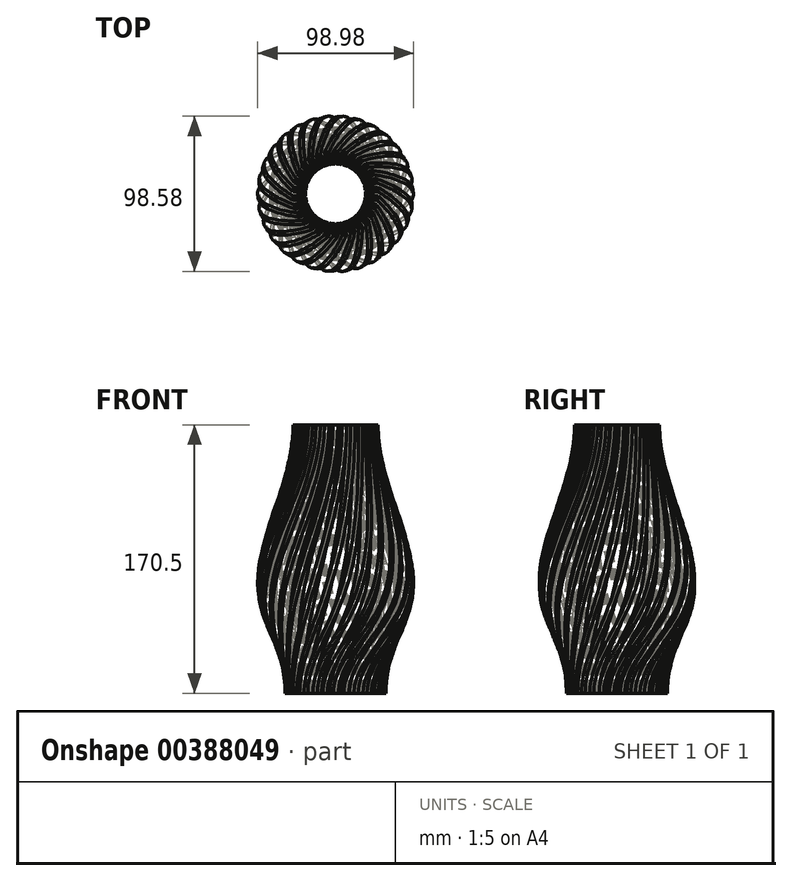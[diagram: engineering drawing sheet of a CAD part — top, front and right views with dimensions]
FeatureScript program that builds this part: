
annotation { "Feature Type Name" : "Feature", "Feature Type Description" : "" }
export const myFeature = defineFeature(function(context is Context, id is Id, definition is map)
    precondition{}
    {
        {
            var Q0;
            Q0=qCreatedBy(makeId("Top.planeOp"),FACE);
            var sketch = newSketch(context, id + "F0", { "sketchPlane" : qUnion([Q0])});
            skCircle(sketch, "E0", {"center": v(0, 0) * mm, "radius": 25 * mm});
            skLineSegment(sketch, "E1", {"start": v(-1.5, 24.95) * mm, "end": v(-1.5, 31.95) * mm});
            skLineSegment(sketch, "E2", {"start": v(-1.5, 31.95) * mm, "end": v(1.5, 31.95) * mm});
            skLineSegment(sketch, "E3", {"start": v(1.5, 31.95) * mm, "end": v(1.5, 24.95) * mm});
            skLineSegment(sketch, "E4", {"start": v(0, 25) * mm, "end": v(0, 35.88) * mm, "construction": true});
            skLineSegment(sketch, "E5.1.0", {"start": v(-5.18, 31.57) * mm, "end": v(-3.72, 24.72) * mm});
            skLineSegment(sketch, "E5.1.1", {"start": v(-8.11, 30.94) * mm, "end": v(-5.18, 31.57) * mm});
            skLineSegment(sketch, "E5.1.2", {"start": v(-6.66, 24.1) * mm, "end": v(-8.11, 30.94) * mm});
            skLineSegment(sketch, "E5.2.0", {"start": v(-11.63, 29.8) * mm, "end": v(-8.78, 23.4) * mm});
            skLineSegment(sketch, "E5.2.1", {"start": v(-14.37, 28.58) * mm, "end": v(-11.63, 29.8) * mm});
            skLineSegment(sketch, "E5.2.2", {"start": v(-11.52, 22.19) * mm, "end": v(-14.37, 28.58) * mm});
            skLineSegment(sketch, "E5.3.0", {"start": v(-17.57, 26.73) * mm, "end": v(-13.45, 21.07) * mm});
            skLineSegment(sketch, "E5.3.1", {"start": v(-20, 24.97) * mm, "end": v(-17.57, 26.73) * mm});
            skLineSegment(sketch, "E5.3.2", {"start": v(-15.88, 19.3) * mm, "end": v(-20, 24.97) * mm});
            skLineSegment(sketch, "E5.4.0", {"start": v(-22.74, 22.5) * mm, "end": v(-17.54, 17.81) * mm});
            skLineSegment(sketch, "E5.4.1", {"start": v(-24.75, 20.27) * mm, "end": v(-22.74, 22.5) * mm});
            skLineSegment(sketch, "E5.4.2", {"start": v(-19.55, 15.58) * mm, "end": v(-24.75, 20.27) * mm});
            skLineSegment(sketch, "E5.5.0", {"start": v(-26.92, 17.28) * mm, "end": v(-20.86, 13.78) * mm});
            skLineSegment(sketch, "E5.5.1", {"start": v(-28.42, 14.68) * mm, "end": v(-26.92, 17.28) * mm});
            skLineSegment(sketch, "E5.5.2", {"start": v(-22.36, 11.18) * mm, "end": v(-28.42, 14.68) * mm});
            skLineSegment(sketch, "E5.6.0", {"start": v(-29.93, 11.3) * mm, "end": v(-23.27, 9.14) * mm});
            skLineSegment(sketch, "E5.6.1", {"start": v(-30.85, 8.45) * mm, "end": v(-29.93, 11.3) * mm});
            skLineSegment(sketch, "E5.6.2", {"start": v(-24.2, 6.28) * mm, "end": v(-30.85, 8.45) * mm});
            skLineSegment(sketch, "E5.7.0", {"start": v(-31.62, 4.83) * mm, "end": v(-24.66, 4.1) * mm});
            skLineSegment(sketch, "E5.7.1", {"start": v(-31.94, 1.85) * mm, "end": v(-31.62, 4.83) * mm});
            skLineSegment(sketch, "E5.7.2", {"start": v(-24.98, 1.12) * mm, "end": v(-31.94, 1.85) * mm});
            skLineSegment(sketch, "E5.8.0", {"start": v(-31.94, -1.85) * mm, "end": v(-24.98, -1.12) * mm});
            skLineSegment(sketch, "E5.8.1", {"start": v(-31.62, -4.83) * mm, "end": v(-31.94, -1.85) * mm});
            skLineSegment(sketch, "E5.8.2", {"start": v(-24.66, -4.1) * mm, "end": v(-31.62, -4.83) * mm});
            skLineSegment(sketch, "E5.9.0", {"start": v(-30.85, -8.45) * mm, "end": v(-24.2, -6.28) * mm});
            skLineSegment(sketch, "E5.9.1", {"start": v(-29.93, -11.3) * mm, "end": v(-30.85, -8.45) * mm});
            skLineSegment(sketch, "E5.9.2", {"start": v(-23.27, -9.14) * mm, "end": v(-29.93, -11.3) * mm});
            skLineSegment(sketch, "E5.10.0", {"start": v(-28.42, -14.68) * mm, "end": v(-22.36, -11.18) * mm});
            skLineSegment(sketch, "E5.10.1", {"start": v(-26.92, -17.28) * mm, "end": v(-28.42, -14.68) * mm});
            skLineSegment(sketch, "E5.10.2", {"start": v(-20.86, -13.78) * mm, "end": v(-26.92, -17.28) * mm});
            skLineSegment(sketch, "E5.11.0", {"start": v(-24.75, -20.27) * mm, "end": v(-19.55, -15.58) * mm});
            skLineSegment(sketch, "E5.11.1", {"start": v(-22.74, -22.5) * mm, "end": v(-24.75, -20.27) * mm});
            skLineSegment(sketch, "E5.11.2", {"start": v(-17.54, -17.81) * mm, "end": v(-22.74, -22.5) * mm});
            skLineSegment(sketch, "E5.12.0", {"start": v(-20, -24.97) * mm, "end": v(-15.88, -19.3) * mm});
            skLineSegment(sketch, "E5.12.1", {"start": v(-17.57, -26.73) * mm, "end": v(-20, -24.97) * mm});
            skLineSegment(sketch, "E5.12.2", {"start": v(-13.45, -21.07) * mm, "end": v(-17.57, -26.73) * mm});
            skLineSegment(sketch, "E5.13.0", {"start": v(-14.37, -28.58) * mm, "end": v(-11.52, -22.19) * mm});
            skLineSegment(sketch, "E5.13.1", {"start": v(-11.63, -29.8) * mm, "end": v(-14.37, -28.58) * mm});
            skLineSegment(sketch, "E5.13.2", {"start": v(-8.78, -23.4) * mm, "end": v(-11.63, -29.8) * mm});
            skLineSegment(sketch, "E5.14.0", {"start": v(-8.11, -30.94) * mm, "end": v(-6.66, -24.1) * mm});
            skLineSegment(sketch, "E5.14.1", {"start": v(-5.18, -31.57) * mm, "end": v(-8.11, -30.94) * mm});
            skLineSegment(sketch, "E5.14.2", {"start": v(-3.72, -24.72) * mm, "end": v(-5.18, -31.57) * mm});
            skLineSegment(sketch, "E6.2.15.0", {"start": v(-1.5, -31.95) * mm, "end": v(-1.5, -24.95) * mm});
            skLineSegment(sketch, "E6.3.15.0", {"start": v(1.5, -31.95) * mm, "end": v(-1.5, -31.95) * mm});
            skLineSegment(sketch, "E6.6.15.0", {"start": v(1.5, -24.95) * mm, "end": v(1.5, -31.95) * mm});
            skLineSegment(sketch, "E6.2.16.0", {"start": v(5.18, -31.57) * mm, "end": v(3.72, -24.72) * mm});
            skLineSegment(sketch, "E6.3.16.0", {"start": v(8.11, -30.94) * mm, "end": v(5.18, -31.57) * mm});
            skLineSegment(sketch, "E6.6.16.0", {"start": v(6.66, -24.1) * mm, "end": v(8.11, -30.94) * mm});
            skLineSegment(sketch, "E6.2.17.0", {"start": v(11.63, -29.8) * mm, "end": v(8.78, -23.4) * mm});
            skLineSegment(sketch, "E6.3.17.0", {"start": v(14.37, -28.58) * mm, "end": v(11.63, -29.8) * mm});
            skLineSegment(sketch, "E6.6.17.0", {"start": v(11.52, -22.19) * mm, "end": v(14.37, -28.58) * mm});
            skLineSegment(sketch, "E6.2.18.0", {"start": v(17.57, -26.73) * mm, "end": v(13.45, -21.07) * mm});
            skLineSegment(sketch, "E6.3.18.0", {"start": v(20, -24.97) * mm, "end": v(17.57, -26.73) * mm});
            skLineSegment(sketch, "E6.6.18.0", {"start": v(15.88, -19.3) * mm, "end": v(20, -24.97) * mm});
            skLineSegment(sketch, "E6.2.19.0", {"start": v(22.74, -22.5) * mm, "end": v(17.54, -17.81) * mm});
            skLineSegment(sketch, "E6.3.19.0", {"start": v(24.75, -20.27) * mm, "end": v(22.74, -22.5) * mm});
            skLineSegment(sketch, "E6.6.19.0", {"start": v(19.55, -15.58) * mm, "end": v(24.75, -20.27) * mm});
            skLineSegment(sketch, "E7.2.20.0", {"start": v(26.92, -17.28) * mm, "end": v(20.86, -13.78) * mm});
            skLineSegment(sketch, "E7.3.20.0", {"start": v(28.42, -14.68) * mm, "end": v(26.92, -17.28) * mm});
            skLineSegment(sketch, "E7.6.20.0", {"start": v(22.36, -11.18) * mm, "end": v(28.42, -14.68) * mm});
            skLineSegment(sketch, "E7.2.21.0", {"start": v(29.93, -11.3) * mm, "end": v(23.27, -9.14) * mm});
            skLineSegment(sketch, "E7.3.21.0", {"start": v(30.85, -8.45) * mm, "end": v(29.93, -11.3) * mm});
            skLineSegment(sketch, "E7.6.21.0", {"start": v(24.2, -6.28) * mm, "end": v(30.85, -8.45) * mm});
            skLineSegment(sketch, "E7.2.22.0", {"start": v(31.62, -4.83) * mm, "end": v(24.66, -4.1) * mm});
            skLineSegment(sketch, "E7.3.22.0", {"start": v(31.94, -1.85) * mm, "end": v(31.62, -4.83) * mm});
            skLineSegment(sketch, "E7.6.22.0", {"start": v(24.98, -1.12) * mm, "end": v(31.94, -1.85) * mm});
            skLineSegment(sketch, "E7.2.23.0", {"start": v(31.94, 1.85) * mm, "end": v(24.98, 1.12) * mm});
            skLineSegment(sketch, "E7.3.23.0", {"start": v(31.62, 4.83) * mm, "end": v(31.94, 1.85) * mm});
            skLineSegment(sketch, "E7.6.23.0", {"start": v(24.66, 4.1) * mm, "end": v(31.62, 4.83) * mm});
            skLineSegment(sketch, "E7.2.24.0", {"start": v(30.85, 8.45) * mm, "end": v(24.2, 6.28) * mm});
            skLineSegment(sketch, "E7.3.24.0", {"start": v(29.93, 11.3) * mm, "end": v(30.85, 8.45) * mm});
            skLineSegment(sketch, "E7.6.24.0", {"start": v(23.27, 9.14) * mm, "end": v(29.93, 11.3) * mm});
            skLineSegment(sketch, "E8.2.25.0", {"start": v(28.42, 14.68) * mm, "end": v(22.36, 11.18) * mm});
            skLineSegment(sketch, "E8.3.25.0", {"start": v(26.92, 17.28) * mm, "end": v(28.42, 14.68) * mm});
            skLineSegment(sketch, "E8.6.25.0", {"start": v(20.86, 13.78) * mm, "end": v(26.92, 17.28) * mm});
            skLineSegment(sketch, "E8.2.26.0", {"start": v(24.75, 20.27) * mm, "end": v(19.55, 15.58) * mm});
            skLineSegment(sketch, "E8.3.26.0", {"start": v(22.74, 22.5) * mm, "end": v(24.75, 20.27) * mm});
            skLineSegment(sketch, "E8.6.26.0", {"start": v(17.54, 17.81) * mm, "end": v(22.74, 22.5) * mm});
            skLineSegment(sketch, "E8.2.27.0", {"start": v(20, 24.97) * mm, "end": v(15.88, 19.3) * mm});
            skLineSegment(sketch, "E8.3.27.0", {"start": v(17.57, 26.73) * mm, "end": v(20, 24.97) * mm});
            skLineSegment(sketch, "E8.6.27.0", {"start": v(13.45, 21.07) * mm, "end": v(17.57, 26.73) * mm});
            skLineSegment(sketch, "E8.2.28.0", {"start": v(14.37, 28.58) * mm, "end": v(11.52, 22.19) * mm});
            skLineSegment(sketch, "E8.3.28.0", {"start": v(11.63, 29.8) * mm, "end": v(14.37, 28.58) * mm});
            skLineSegment(sketch, "E8.6.28.0", {"start": v(8.78, 23.4) * mm, "end": v(11.63, 29.8) * mm});
            skLineSegment(sketch, "E8.2.29.0", {"start": v(8.11, 30.94) * mm, "end": v(6.66, 24.1) * mm});
            skLineSegment(sketch, "E8.3.29.0", {"start": v(5.18, 31.57) * mm, "end": v(8.11, 30.94) * mm});
            skLineSegment(sketch, "E8.6.29.0", {"start": v(3.72, 24.72) * mm, "end": v(5.18, 31.57) * mm});
            skSolve(sketch);
        }
        {
            var Q0;
            Q0=qCreatedBy(makeId("Top.planeOp"),FACE);
            cPlane(context, id + "F1", {"entities" : qUnion([Q0]), "cplaneType" : CPlaneType.OFFSET, "offset" : 52.5 * mm, "width" : 150 * mm, "height" : 150 * mm});
        }
        {
            var Q0;
            Q0=qCreatedBy(id+"F1.planeOp",FACE);
            cPlane(context, id + "F2", {"entities" : qUnion([Q0]), "cplaneType" : CPlaneType.OFFSET, "offset" : 25 * mm, "width" : 150 * mm, "height" : 150 * mm});
        }
        {
            var Q0;
            Q0=qCreatedBy(id+"F1.planeOp",FACE);
            var sketch = newSketch(context, id + "F3", { "sketchPlane" : qUnion([Q0])});
            skCircle(sketch, "E9", {"center": v(0, 0) * mm, "radius": 40 * mm});
            skLineSegment(sketch, "E10", {"start": v(-1.5, 39.97) * mm, "end": v(-1.5, 46.97) * mm});
            skLineSegment(sketch, "E11", {"start": v(-1.5, 46.97) * mm, "end": v(1.5, 46.97) * mm});
            skLineSegment(sketch, "E12", {"start": v(1.5, 46.97) * mm, "end": v(1.5, 39.97) * mm});
            skLineSegment(sketch, "E13", {"start": v(0, 40) * mm, "end": v(0, 44.41) * mm, "construction": true});
            skLineSegment(sketch, "E14.1.0", {"start": v(-8.3, 46.26) * mm, "end": v(-6.84, 39.41) * mm});
            skLineSegment(sketch, "E14.1.1", {"start": v(-11.23, 45.63) * mm, "end": v(-8.3, 46.26) * mm});
            skLineSegment(sketch, "E14.1.2", {"start": v(-9.78, 38.79) * mm, "end": v(-11.23, 45.63) * mm});
            skLineSegment(sketch, "E14.2.0", {"start": v(-17.73, 43.52) * mm, "end": v(-14.89, 37.13) * mm});
            skLineSegment(sketch, "E14.2.1", {"start": v(-20.48, 42.3) * mm, "end": v(-17.73, 43.52) * mm});
            skLineSegment(sketch, "E14.2.2", {"start": v(-17.63, 35.9) * mm, "end": v(-20.48, 42.3) * mm});
            skLineSegment(sketch, "E14.3.0", {"start": v(-26.4, 38.88) * mm, "end": v(-22.28, 33.22) * mm});
            skLineSegment(sketch, "E14.3.1", {"start": v(-28.82, 37.12) * mm, "end": v(-26.4, 38.88) * mm});
            skLineSegment(sketch, "E14.3.2", {"start": v(-24.7, 31.46) * mm, "end": v(-28.82, 37.12) * mm});
            skLineSegment(sketch, "E14.4.0", {"start": v(-33.9, 32.55) * mm, "end": v(-28.7, 27.86) * mm});
            skLineSegment(sketch, "E14.4.1", {"start": v(-35.91, 30.32) * mm, "end": v(-33.9, 32.55) * mm});
            skLineSegment(sketch, "E14.4.2", {"start": v(-30.7, 25.63) * mm, "end": v(-35.91, 30.32) * mm});
            skLineSegment(sketch, "E14.5.0", {"start": v(-39.93, 24.78) * mm, "end": v(-33.87, 21.28) * mm});
            skLineSegment(sketch, "E14.5.1", {"start": v(-41.43, 22.19) * mm, "end": v(-39.93, 24.78) * mm});
            skLineSegment(sketch, "E14.5.2", {"start": v(-35.37, 18.69) * mm, "end": v(-41.43, 22.19) * mm});
            skLineSegment(sketch, "E14.6.0", {"start": v(-44.2, 15.94) * mm, "end": v(-37.55, 13.78) * mm});
            skLineSegment(sketch, "E14.6.1", {"start": v(-45.14, 13.09) * mm, "end": v(-44.2, 15.94) * mm});
            skLineSegment(sketch, "E14.6.2", {"start": v(-38.48, 10.93) * mm, "end": v(-45.14, 13.09) * mm});
            skLineSegment(sketch, "E14.7.0", {"start": v(-46.56, 6.4) * mm, "end": v(-39.6, 5.67) * mm});
            skLineSegment(sketch, "E14.7.1", {"start": v(-46.87, 3.42) * mm, "end": v(-46.56, 6.4) * mm});
            skLineSegment(sketch, "E14.7.2", {"start": v(-39.9, 2.69) * mm, "end": v(-46.87, 3.42) * mm});
            skLineSegment(sketch, "E14.8.0", {"start": v(-46.87, -3.42) * mm, "end": v(-39.9, -2.69) * mm});
            skLineSegment(sketch, "E14.8.1", {"start": v(-46.56, -6.4) * mm, "end": v(-46.87, -3.42) * mm});
            skLineSegment(sketch, "E14.8.2", {"start": v(-39.6, -5.67) * mm, "end": v(-46.56, -6.4) * mm});
            skLineSegment(sketch, "E14.9.0", {"start": v(-45.14, -13.09) * mm, "end": v(-38.48, -10.93) * mm});
            skLineSegment(sketch, "E14.9.1", {"start": v(-44.2, -15.94) * mm, "end": v(-45.14, -13.09) * mm});
            skLineSegment(sketch, "E14.9.2", {"start": v(-37.55, -13.78) * mm, "end": v(-44.2, -15.94) * mm});
            skLineSegment(sketch, "E14.10.0", {"start": v(-41.43, -22.19) * mm, "end": v(-35.37, -18.69) * mm});
            skLineSegment(sketch, "E14.10.1", {"start": v(-39.93, -24.78) * mm, "end": v(-41.43, -22.19) * mm});
            skLineSegment(sketch, "E14.10.2", {"start": v(-33.87, -21.28) * mm, "end": v(-39.93, -24.78) * mm});
            skLineSegment(sketch, "E14.11.0", {"start": v(-35.91, -30.32) * mm, "end": v(-30.7, -25.63) * mm});
            skLineSegment(sketch, "E14.11.1", {"start": v(-33.9, -32.55) * mm, "end": v(-35.91, -30.32) * mm});
            skLineSegment(sketch, "E14.11.2", {"start": v(-28.7, -27.86) * mm, "end": v(-33.9, -32.55) * mm});
            skLineSegment(sketch, "E14.12.0", {"start": v(-28.82, -37.12) * mm, "end": v(-24.7, -31.46) * mm});
            skLineSegment(sketch, "E14.12.1", {"start": v(-26.4, -38.88) * mm, "end": v(-28.82, -37.12) * mm});
            skLineSegment(sketch, "E14.12.2", {"start": v(-22.28, -33.22) * mm, "end": v(-26.4, -38.88) * mm});
            skLineSegment(sketch, "E14.13.0", {"start": v(-20.48, -42.3) * mm, "end": v(-17.63, -35.9) * mm});
            skLineSegment(sketch, "E14.13.1", {"start": v(-17.73, -43.52) * mm, "end": v(-20.48, -42.3) * mm});
            skLineSegment(sketch, "E14.13.2", {"start": v(-14.89, -37.13) * mm, "end": v(-17.73, -43.52) * mm});
            skLineSegment(sketch, "E14.14.0", {"start": v(-11.23, -45.63) * mm, "end": v(-9.78, -38.79) * mm});
            skLineSegment(sketch, "E14.14.1", {"start": v(-8.3, -46.26) * mm, "end": v(-11.23, -45.63) * mm});
            skLineSegment(sketch, "E14.14.2", {"start": v(-6.84, -39.41) * mm, "end": v(-8.3, -46.26) * mm});
            skLineSegment(sketch, "E15.2.15.0", {"start": v(-1.5, -46.97) * mm, "end": v(-1.5, -39.97) * mm});
            skLineSegment(sketch, "E15.3.15.0", {"start": v(1.5, -46.97) * mm, "end": v(-1.5, -46.97) * mm});
            skLineSegment(sketch, "E15.6.15.0", {"start": v(1.5, -39.97) * mm, "end": v(1.5, -46.97) * mm});
            skLineSegment(sketch, "E15.2.16.0", {"start": v(8.3, -46.26) * mm, "end": v(6.84, -39.41) * mm});
            skLineSegment(sketch, "E15.3.16.0", {"start": v(11.23, -45.63) * mm, "end": v(8.3, -46.26) * mm});
            skLineSegment(sketch, "E15.6.16.0", {"start": v(9.78, -38.79) * mm, "end": v(11.23, -45.63) * mm});
            skLineSegment(sketch, "E15.2.17.0", {"start": v(17.73, -43.52) * mm, "end": v(14.89, -37.13) * mm});
            skLineSegment(sketch, "E15.3.17.0", {"start": v(20.48, -42.3) * mm, "end": v(17.73, -43.52) * mm});
            skLineSegment(sketch, "E15.6.17.0", {"start": v(17.63, -35.9) * mm, "end": v(20.48, -42.3) * mm});
            skLineSegment(sketch, "E15.2.18.0", {"start": v(26.4, -38.88) * mm, "end": v(22.28, -33.22) * mm});
            skLineSegment(sketch, "E15.3.18.0", {"start": v(28.82, -37.12) * mm, "end": v(26.4, -38.88) * mm});
            skLineSegment(sketch, "E15.6.18.0", {"start": v(24.7, -31.46) * mm, "end": v(28.82, -37.12) * mm});
            skLineSegment(sketch, "E15.2.19.0", {"start": v(33.9, -32.55) * mm, "end": v(28.7, -27.86) * mm});
            skLineSegment(sketch, "E15.3.19.0", {"start": v(35.91, -30.32) * mm, "end": v(33.9, -32.55) * mm});
            skLineSegment(sketch, "E15.6.19.0", {"start": v(30.7, -25.63) * mm, "end": v(35.91, -30.32) * mm});
            skLineSegment(sketch, "E16.2.20.0", {"start": v(39.93, -24.78) * mm, "end": v(33.87, -21.28) * mm});
            skLineSegment(sketch, "E16.3.20.0", {"start": v(41.43, -22.19) * mm, "end": v(39.93, -24.78) * mm});
            skLineSegment(sketch, "E16.6.20.0", {"start": v(35.37, -18.69) * mm, "end": v(41.43, -22.19) * mm});
            skLineSegment(sketch, "E16.2.21.0", {"start": v(44.2, -15.94) * mm, "end": v(37.55, -13.78) * mm});
            skLineSegment(sketch, "E16.3.21.0", {"start": v(45.14, -13.09) * mm, "end": v(44.2, -15.94) * mm});
            skLineSegment(sketch, "E16.6.21.0", {"start": v(38.48, -10.93) * mm, "end": v(45.14, -13.09) * mm});
            skLineSegment(sketch, "E16.2.22.0", {"start": v(46.56, -6.4) * mm, "end": v(39.6, -5.67) * mm});
            skLineSegment(sketch, "E16.3.22.0", {"start": v(46.87, -3.42) * mm, "end": v(46.56, -6.4) * mm});
            skLineSegment(sketch, "E16.6.22.0", {"start": v(39.9, -2.69) * mm, "end": v(46.87, -3.42) * mm});
            skLineSegment(sketch, "E16.2.23.0", {"start": v(46.87, 3.42) * mm, "end": v(39.9, 2.69) * mm});
            skLineSegment(sketch, "E16.3.23.0", {"start": v(46.56, 6.4) * mm, "end": v(46.87, 3.42) * mm});
            skLineSegment(sketch, "E16.6.23.0", {"start": v(39.6, 5.67) * mm, "end": v(46.56, 6.4) * mm});
            skLineSegment(sketch, "E16.2.24.0", {"start": v(45.14, 13.09) * mm, "end": v(38.48, 10.93) * mm});
            skLineSegment(sketch, "E16.3.24.0", {"start": v(44.2, 15.94) * mm, "end": v(45.14, 13.09) * mm});
            skLineSegment(sketch, "E16.6.24.0", {"start": v(37.55, 13.78) * mm, "end": v(44.2, 15.94) * mm});
            skLineSegment(sketch, "E17.2.25.0", {"start": v(41.43, 22.19) * mm, "end": v(35.37, 18.69) * mm});
            skLineSegment(sketch, "E17.3.25.0", {"start": v(39.93, 24.78) * mm, "end": v(41.43, 22.19) * mm});
            skLineSegment(sketch, "E17.6.25.0", {"start": v(33.87, 21.28) * mm, "end": v(39.93, 24.78) * mm});
            skLineSegment(sketch, "E17.2.26.0", {"start": v(35.91, 30.32) * mm, "end": v(30.7, 25.63) * mm});
            skLineSegment(sketch, "E17.3.26.0", {"start": v(33.9, 32.55) * mm, "end": v(35.91, 30.32) * mm});
            skLineSegment(sketch, "E17.6.26.0", {"start": v(28.7, 27.86) * mm, "end": v(33.9, 32.55) * mm});
            skLineSegment(sketch, "E17.2.27.0", {"start": v(28.82, 37.12) * mm, "end": v(24.7, 31.46) * mm});
            skLineSegment(sketch, "E17.3.27.0", {"start": v(26.4, 38.88) * mm, "end": v(28.82, 37.12) * mm});
            skLineSegment(sketch, "E17.6.27.0", {"start": v(22.28, 33.22) * mm, "end": v(26.4, 38.88) * mm});
            skLineSegment(sketch, "E17.2.28.0", {"start": v(20.48, 42.3) * mm, "end": v(17.63, 35.9) * mm});
            skLineSegment(sketch, "E17.3.28.0", {"start": v(17.73, 43.52) * mm, "end": v(20.48, 42.3) * mm});
            skLineSegment(sketch, "E17.6.28.0", {"start": v(14.89, 37.13) * mm, "end": v(17.73, 43.52) * mm});
            skLineSegment(sketch, "E17.2.29.0", {"start": v(11.23, 45.63) * mm, "end": v(9.78, 38.79) * mm});
            skLineSegment(sketch, "E17.3.29.0", {"start": v(8.3, 46.26) * mm, "end": v(11.23, 45.63) * mm});
            skLineSegment(sketch, "E17.6.29.0", {"start": v(6.84, 39.41) * mm, "end": v(8.3, 46.26) * mm});
            skSolve(sketch);
        }
        {
            var Q0;
            Q0=qCreatedBy(id+"F2.planeOp",FACE);
            cPlane(context, id + "F4", {"entities" : qUnion([Q0]), "cplaneType" : CPlaneType.OFFSET, "offset" : 93 * mm, "width" : 150 * mm, "height" : 150 * mm});
        }
        {
            var Q0;
            Q0=qCreatedBy(id+"F4.planeOp",FACE);
            var sketch = newSketch(context, id + "F5", { "sketchPlane" : qUnion([Q0])});
            skCircle(sketch, "E18", {"center": v(0, 0) * mm, "radius": 20 * mm});
            skLineSegment(sketch, "E19", {"start": v(-1.5, 19.94) * mm, "end": v(-1.5, 26.94) * mm});
            skLineSegment(sketch, "E20", {"start": v(-1.5, 26.94) * mm, "end": v(1.5, 26.94) * mm});
            skLineSegment(sketch, "E21", {"start": v(1.5, 26.94) * mm, "end": v(1.5, 19.94) * mm});
            skLineSegment(sketch, "E22", {"start": v(0, 20) * mm, "end": v(0, 35.1) * mm, "construction": true});
            skLineSegment(sketch, "E23.1.0", {"start": v(-4.13, 26.67) * mm, "end": v(-2.68, 19.82) * mm});
            skLineSegment(sketch, "E23.1.1", {"start": v(-7.07, 26.04) * mm, "end": v(-4.13, 26.67) * mm});
            skLineSegment(sketch, "E23.1.2", {"start": v(-5.61, 19.2) * mm, "end": v(-7.07, 26.04) * mm});
            skLineSegment(sketch, "E23.2.0", {"start": v(-9.59, 25.22) * mm, "end": v(-6.74, 18.83) * mm});
            skLineSegment(sketch, "E23.2.1", {"start": v(-12.33, 24) * mm, "end": v(-9.59, 25.22) * mm});
            skLineSegment(sketch, "E23.2.2", {"start": v(-9.48, 17.6) * mm, "end": v(-12.33, 24) * mm});
            skLineSegment(sketch, "E23.3.0", {"start": v(-14.62, 22.68) * mm, "end": v(-10.5, 17.02) * mm});
            skLineSegment(sketch, "E23.3.1", {"start": v(-17.05, 20.92) * mm, "end": v(-14.62, 22.68) * mm});
            skLineSegment(sketch, "E23.3.2", {"start": v(-12.94, 15.25) * mm, "end": v(-17.05, 20.92) * mm});
            skLineSegment(sketch, "E23.4.0", {"start": v(-19.02, 19.14) * mm, "end": v(-13.82, 14.46) * mm});
            skLineSegment(sketch, "E23.4.1", {"start": v(-21.03, 16.91) * mm, "end": v(-19.02, 19.14) * mm});
            skLineSegment(sketch, "E23.4.2", {"start": v(-15.82, 12.23) * mm, "end": v(-21.03, 16.91) * mm});
            skLineSegment(sketch, "E23.5.0", {"start": v(-22.58, 14.77) * mm, "end": v(-16.52, 11.27) * mm});
            skLineSegment(sketch, "E23.5.1", {"start": v(-24.08, 12.17) * mm, "end": v(-22.58, 14.77) * mm});
            skLineSegment(sketch, "E23.5.2", {"start": v(-18.02, 8.67) * mm, "end": v(-24.08, 12.17) * mm});
            skLineSegment(sketch, "E23.6.0", {"start": v(-25.16, 9.75) * mm, "end": v(-18.5, 7.59) * mm});
            skLineSegment(sketch, "E23.6.1", {"start": v(-26.09, 6.9) * mm, "end": v(-25.16, 9.75) * mm});
            skLineSegment(sketch, "E23.6.2", {"start": v(-19.43, 4.74) * mm, "end": v(-26.09, 6.9) * mm});
            skLineSegment(sketch, "E23.7.0", {"start": v(-26.64, 4.3) * mm, "end": v(-19.68, 3.58) * mm});
            skLineSegment(sketch, "E23.7.1", {"start": v(-26.95, 1.32) * mm, "end": v(-26.64, 4.3) * mm});
            skLineSegment(sketch, "E23.7.2", {"start": v(-20, 0.6) * mm, "end": v(-26.95, 1.32) * mm});
            skLineSegment(sketch, "E23.8.0", {"start": v(-26.95, -1.32) * mm, "end": v(-20, -0.6) * mm});
            skLineSegment(sketch, "E23.8.1", {"start": v(-26.64, -4.3) * mm, "end": v(-26.95, -1.32) * mm});
            skLineSegment(sketch, "E23.8.2", {"start": v(-19.68, -3.58) * mm, "end": v(-26.64, -4.3) * mm});
            skLineSegment(sketch, "E23.9.0", {"start": v(-26.09, -6.9) * mm, "end": v(-19.43, -4.74) * mm});
            skLineSegment(sketch, "E23.9.1", {"start": v(-25.16, -9.75) * mm, "end": v(-26.09, -6.9) * mm});
            skLineSegment(sketch, "E23.9.2", {"start": v(-18.5, -7.59) * mm, "end": v(-25.16, -9.75) * mm});
            skLineSegment(sketch, "E23.10.0", {"start": v(-24.08, -12.17) * mm, "end": v(-18.02, -8.67) * mm});
            skLineSegment(sketch, "E23.10.1", {"start": v(-22.58, -14.77) * mm, "end": v(-24.08, -12.17) * mm});
            skLineSegment(sketch, "E23.10.2", {"start": v(-16.52, -11.27) * mm, "end": v(-22.58, -14.77) * mm});
            skLineSegment(sketch, "E23.11.0", {"start": v(-21.03, -16.91) * mm, "end": v(-15.82, -12.23) * mm});
            skLineSegment(sketch, "E23.11.1", {"start": v(-19.02, -19.14) * mm, "end": v(-21.03, -16.91) * mm});
            skLineSegment(sketch, "E23.11.2", {"start": v(-13.82, -14.46) * mm, "end": v(-19.02, -19.14) * mm});
            skLineSegment(sketch, "E23.12.0", {"start": v(-17.05, -20.92) * mm, "end": v(-12.94, -15.25) * mm});
            skLineSegment(sketch, "E23.12.1", {"start": v(-14.62, -22.68) * mm, "end": v(-17.05, -20.92) * mm});
            skLineSegment(sketch, "E23.12.2", {"start": v(-10.5, -17.02) * mm, "end": v(-14.62, -22.68) * mm});
            skLineSegment(sketch, "E23.13.0", {"start": v(-12.33, -24) * mm, "end": v(-9.48, -17.6) * mm});
            skLineSegment(sketch, "E23.13.1", {"start": v(-9.59, -25.22) * mm, "end": v(-12.33, -24) * mm});
            skLineSegment(sketch, "E23.13.2", {"start": v(-6.74, -18.83) * mm, "end": v(-9.59, -25.22) * mm});
            skLineSegment(sketch, "E23.14.0", {"start": v(-7.07, -26.04) * mm, "end": v(-5.61, -19.2) * mm});
            skLineSegment(sketch, "E23.14.1", {"start": v(-4.13, -26.67) * mm, "end": v(-7.07, -26.04) * mm});
            skLineSegment(sketch, "E23.14.2", {"start": v(-2.68, -19.82) * mm, "end": v(-4.13, -26.67) * mm});
            skLineSegment(sketch, "E24.2.15.0", {"start": v(-1.5, -26.94) * mm, "end": v(-1.5, -19.94) * mm});
            skLineSegment(sketch, "E24.3.15.0", {"start": v(1.5, -26.94) * mm, "end": v(-1.5, -26.94) * mm});
            skLineSegment(sketch, "E24.6.15.0", {"start": v(1.5, -19.94) * mm, "end": v(1.5, -26.94) * mm});
            skLineSegment(sketch, "E24.2.16.0", {"start": v(4.13, -26.67) * mm, "end": v(2.68, -19.82) * mm});
            skLineSegment(sketch, "E24.3.16.0", {"start": v(7.07, -26.04) * mm, "end": v(4.13, -26.67) * mm});
            skLineSegment(sketch, "E24.6.16.0", {"start": v(5.61, -19.2) * mm, "end": v(7.07, -26.04) * mm});
            skLineSegment(sketch, "E24.2.17.0", {"start": v(9.59, -25.22) * mm, "end": v(6.74, -18.83) * mm});
            skLineSegment(sketch, "E24.3.17.0", {"start": v(12.33, -24) * mm, "end": v(9.59, -25.22) * mm});
            skLineSegment(sketch, "E24.6.17.0", {"start": v(9.48, -17.6) * mm, "end": v(12.33, -24) * mm});
            skLineSegment(sketch, "E24.2.18.0", {"start": v(14.62, -22.68) * mm, "end": v(10.5, -17.02) * mm});
            skLineSegment(sketch, "E24.3.18.0", {"start": v(17.05, -20.92) * mm, "end": v(14.62, -22.68) * mm});
            skLineSegment(sketch, "E24.6.18.0", {"start": v(12.94, -15.25) * mm, "end": v(17.05, -20.92) * mm});
            skLineSegment(sketch, "E24.2.19.0", {"start": v(19.02, -19.14) * mm, "end": v(13.82, -14.46) * mm});
            skLineSegment(sketch, "E24.3.19.0", {"start": v(21.03, -16.91) * mm, "end": v(19.02, -19.14) * mm});
            skLineSegment(sketch, "E24.6.19.0", {"start": v(15.82, -12.23) * mm, "end": v(21.03, -16.91) * mm});
            skLineSegment(sketch, "E25.2.20.0", {"start": v(22.58, -14.77) * mm, "end": v(16.52, -11.27) * mm});
            skLineSegment(sketch, "E25.3.20.0", {"start": v(24.08, -12.17) * mm, "end": v(22.58, -14.77) * mm});
            skLineSegment(sketch, "E25.6.20.0", {"start": v(18.02, -8.67) * mm, "end": v(24.08, -12.17) * mm});
            skLineSegment(sketch, "E25.2.21.0", {"start": v(25.16, -9.75) * mm, "end": v(18.5, -7.59) * mm});
            skLineSegment(sketch, "E25.3.21.0", {"start": v(26.09, -6.9) * mm, "end": v(25.16, -9.75) * mm});
            skLineSegment(sketch, "E25.6.21.0", {"start": v(19.43, -4.74) * mm, "end": v(26.09, -6.9) * mm});
            skLineSegment(sketch, "E25.2.22.0", {"start": v(26.64, -4.3) * mm, "end": v(19.68, -3.58) * mm});
            skLineSegment(sketch, "E25.3.22.0", {"start": v(26.95, -1.32) * mm, "end": v(26.64, -4.3) * mm});
            skLineSegment(sketch, "E25.6.22.0", {"start": v(20, -0.6) * mm, "end": v(26.95, -1.32) * mm});
            skLineSegment(sketch, "E25.2.23.0", {"start": v(26.95, 1.32) * mm, "end": v(20, 0.6) * mm});
            skLineSegment(sketch, "E25.3.23.0", {"start": v(26.64, 4.3) * mm, "end": v(26.95, 1.32) * mm});
            skLineSegment(sketch, "E25.6.23.0", {"start": v(19.68, 3.58) * mm, "end": v(26.64, 4.3) * mm});
            skLineSegment(sketch, "E25.2.24.0", {"start": v(26.09, 6.9) * mm, "end": v(19.43, 4.74) * mm});
            skLineSegment(sketch, "E25.3.24.0", {"start": v(25.16, 9.75) * mm, "end": v(26.09, 6.9) * mm});
            skLineSegment(sketch, "E25.6.24.0", {"start": v(18.5, 7.59) * mm, "end": v(25.16, 9.75) * mm});
            skLineSegment(sketch, "E26.2.25.0", {"start": v(24.08, 12.17) * mm, "end": v(18.02, 8.67) * mm});
            skLineSegment(sketch, "E26.3.25.0", {"start": v(22.58, 14.77) * mm, "end": v(24.08, 12.17) * mm});
            skLineSegment(sketch, "E26.6.25.0", {"start": v(16.52, 11.27) * mm, "end": v(22.58, 14.77) * mm});
            skLineSegment(sketch, "E26.2.26.0", {"start": v(21.03, 16.91) * mm, "end": v(15.82, 12.23) * mm});
            skLineSegment(sketch, "E26.3.26.0", {"start": v(19.02, 19.14) * mm, "end": v(21.03, 16.91) * mm});
            skLineSegment(sketch, "E26.6.26.0", {"start": v(13.82, 14.46) * mm, "end": v(19.02, 19.14) * mm});
            skLineSegment(sketch, "E26.2.27.0", {"start": v(17.05, 20.92) * mm, "end": v(12.94, 15.25) * mm});
            skLineSegment(sketch, "E26.3.27.0", {"start": v(14.62, 22.68) * mm, "end": v(17.05, 20.92) * mm});
            skLineSegment(sketch, "E26.6.27.0", {"start": v(10.5, 17.02) * mm, "end": v(14.62, 22.68) * mm});
            skLineSegment(sketch, "E26.2.28.0", {"start": v(12.33, 24) * mm, "end": v(9.48, 17.6) * mm});
            skLineSegment(sketch, "E26.3.28.0", {"start": v(9.59, 25.22) * mm, "end": v(12.33, 24) * mm});
            skLineSegment(sketch, "E26.6.28.0", {"start": v(6.74, 18.83) * mm, "end": v(9.59, 25.22) * mm});
            skLineSegment(sketch, "E26.2.29.0", {"start": v(7.07, 26.04) * mm, "end": v(5.61, 19.2) * mm});
            skLineSegment(sketch, "E26.3.29.0", {"start": v(4.13, 26.67) * mm, "end": v(7.07, 26.04) * mm});
            skLineSegment(sketch, "E26.6.29.0", {"start": v(2.68, 19.82) * mm, "end": v(4.13, 26.67) * mm});
            skSolve(sketch);
        }
        {
            var Q0;
            Q0 = qSketchRegion(id + "F0", true);
            var Q1;
            Q1 = qSketchRegion(id + "F3", true);
            var Q2;
            Q2 = qSketchRegion(id + "F5", true);
            var Q3;
            Q3=sQuery(id+"F0.wireOp",VERTEX,"E5.6.2.end");
            var Q4;
            Q4=sQuery(id+"F3.wireOp",VERTEX,"E14.9.1.start");
            var Q5;
            Q5=sQuery(id+"F5.wireOp",VERTEX,"E23.12.2.end");
            loft(context, id + "F6", {"startCondition" : LoftEndDerivativeType.NORMAL_TO_PROFILE, "startMagnitude" : 1, "endCondition" : LoftEndDerivativeType.NORMAL_TO_PROFILE, "endMagnitude" : 1, "sheetProfilesArray" : [{ "sheetProfileEntities" : qUnion([Q0]) }, { "sheetProfileEntities" : qUnion([Q1]) }, { "sheetProfileEntities" : qUnion([Q2]) }], "matchConnections" : true, "connections" : [{ "connectionEntities" : qUnion([Q3, Q4, Q5]), "connectionEdgeQueries" : qUnion([]), "connectionEdgeParameters" : [] }]});
        }
        {
            var Q0;
            {var subQ1=sQuery(id+"F5.wireOp",EDGE,"47b7924f-19fe-41c4-8c08-c64ca53c2e21");var subQ27=sQuery(id+"F5.wireOp",EDGE,"542196b8-f4fa-463c-8464-2ade0f72c37d.10.0");var subQ28=makeQuery(id+"F5.imprint","INTERSECT",VERTEX,{"disambiguationData":[OD(1.0)],"derivedFrom":[subQ1,subQ27]});Q0=makeQuery(id+"F6.opLoft","CAP_FACE",FACE,{"disambiguationData":[OSD([makeQuery(id+"F5.imprint","IMPRINT",FACE,{"disambiguationData":[TD([[makeQuery(id+"F5.imprint","IMPRINT",EDGE,{"disambiguationData":[TD([[subQ28,-1.0]])],"derivedFrom":subQ1}),1.0]])]})])],"isStart":true});}
            var Q1;
            {var subQ0=sQuery(id+"F5.wireOp",EDGE,"E18");var subQ33=makeQuery(id+"F5.imprint","INTERSECT",VERTEX,{"derivedFrom":[subQ0,sQuery(id+"F5.wireOp",EDGE,"E25.2.23.0")]});Q1=makeQuery(id+"F6.opLoft","CAP_FACE",FACE,{"disambiguationData":[OSD([makeQuery(id+"F5.imprint","IMPRINT",FACE,{"disambiguationData":[TD([[makeQuery(id+"F5.imprint","IMPRINT",EDGE,{"disambiguationData":[TD([[subQ33,-1.0]])],"derivedFrom":subQ0}),1.0]])]})])],"isStart":true});}
            shell(context, id + "F7", {"entities" : qUnion([Q0, Q1]), "thickness" : 1 * mm});
        }
    });
